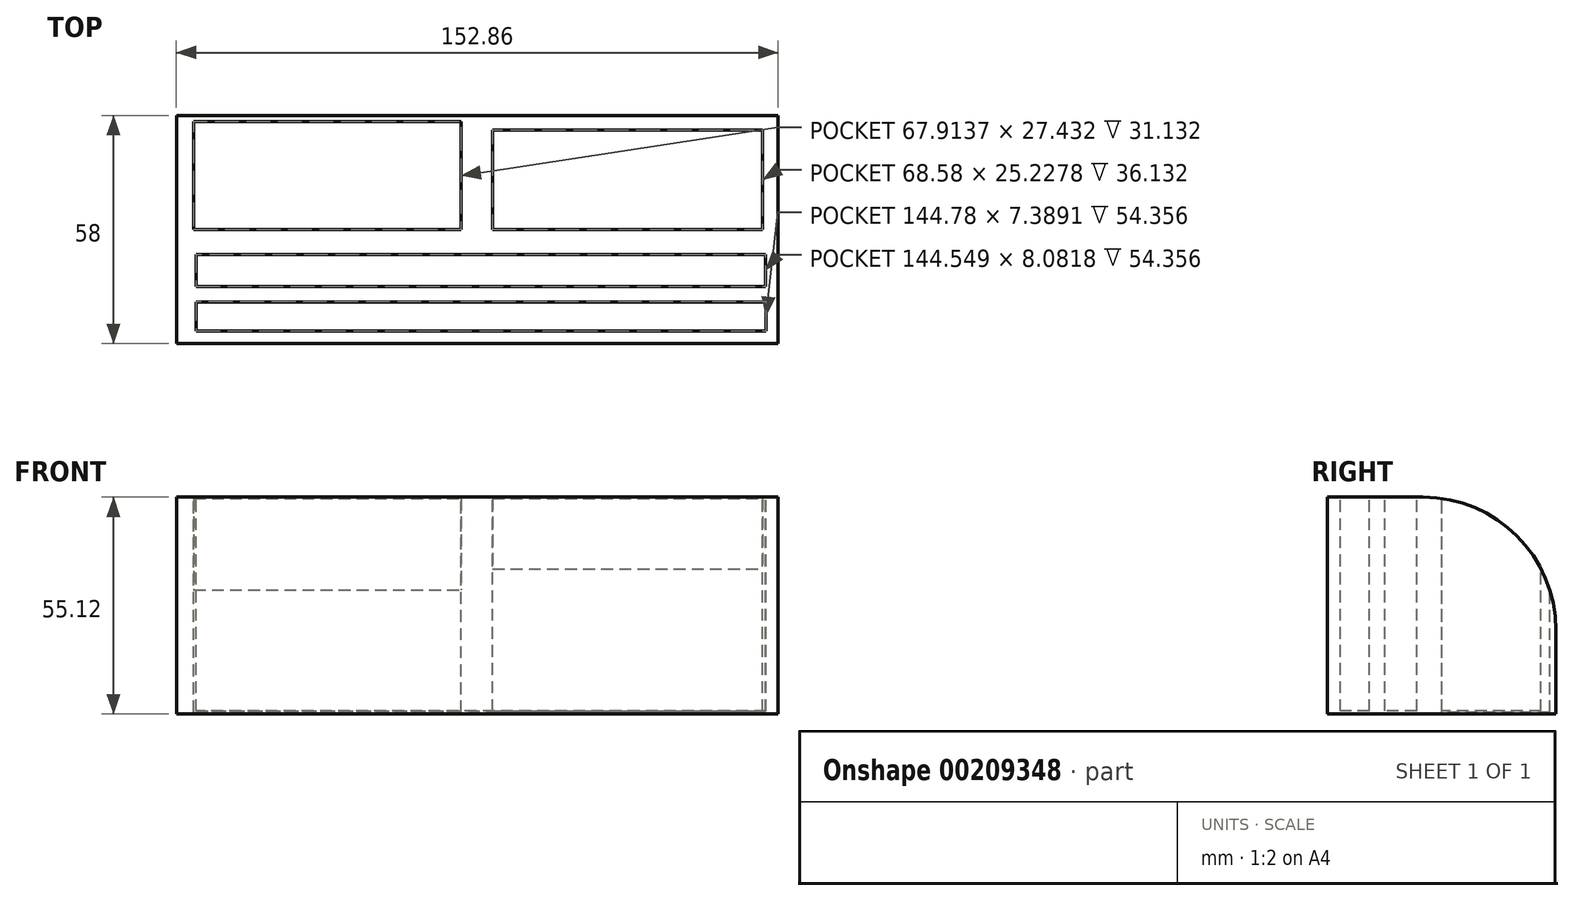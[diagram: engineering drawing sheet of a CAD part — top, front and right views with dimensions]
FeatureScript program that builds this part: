
annotation { "Feature Type Name" : "Feature", "Feature Type Description" : "" }
export const myFeature = defineFeature(function(context is Context, id is Id, definition is map)
    precondition{}
    {
        {
            var Q0;
            Q0=qCreatedBy(makeId("Top.planeOp"),FACE);
            var sketch = newSketch(context, id + "F0", { "sketchPlane" : qUnion([Q0])});
            skLineSegment(sketch, "E0.bottom", {"start": v(-76.43, 29) * mm, "end": v(76.43, 29) * mm});
            skLineSegment(sketch, "E0.top", {"start": v(-76.43, -29) * mm, "end": v(76.43, -29) * mm});
            skLineSegment(sketch, "E0.left", {"start": v(-76.43, 29) * mm, "end": v(-76.43, -29) * mm});
            skLineSegment(sketch, "E0.right", {"start": v(76.43, 29) * mm, "end": v(76.43, -29) * mm});
            skPoint(sketch, "E0.middle", {"position": v(0, 0) * mm});
            skSolve(sketch);
        }
        {
            var Q0;
            Q0=makeQuery(id+"F0.imprint","IMPRINT",FACE,{"disambiguationData":[TD([[makeQuery(id+"F0.imprint","IMPRINT",EDGE,{"derivedFrom":sQuery(id+"F0.wireOp",EDGE,"E0.bottom")}),-1.0]])]});
            extrude(context, id + "F1", {"entities" : qUnion([Q0]), "depth" : 55.12 * mm});
        }
        {
            var Q0;
            Q0=makeQuery(id+"F1.opExtrude","CAP_EDGE",EDGE,{"disambiguationData":[OSD([sQuery(id+"F0.wireOp",EDGE,"E0.bottom")])],"isStart":false});
            fillet(context, id + "F2", {"entities" : qUnion([Q0]), "radius" : 33.73 * mm, "tangentPropagation" : true, "allowEdgeOverflow" : false});
        }
        {
            var Q0;
            Q0=makeQuery(id+"F1.opExtrude","CAP_FACE",FACE,{"disambiguationData":[OSD([sQuery(id+"F0.wireOp",EDGE,"E0.bottom"),sQuery(id+"F0.wireOp",EDGE,"E0.top"),sQuery(id+"F0.wireOp",EDGE,"E0.left"),sQuery(id+"F0.wireOp",EDGE,"E0.right")])],"isStart":false});
            var sketch = newSketch(context, id + "F3", { "sketchPlane" : qUnion([Q0])});
            skLineSegment(sketch, "E1.bottom", {"start": v(-72, 25.23) * mm, "end": v(-4.08, 25.23) * mm});
            skLineSegment(sketch, "E1.top", {"start": v(-72, 0) * mm, "end": v(-4.08, 0) * mm});
            skLineSegment(sketch, "E1.left", {"start": v(-72, 25.23) * mm, "end": v(-72, 0) * mm});
            skLineSegment(sketch, "E1.right", {"start": v(-4.08, 25.23) * mm, "end": v(-4.08, 0) * mm});
            skLineSegment(sketch, "E2.bottom", {"start": v(3.93, 25.23) * mm, "end": v(72.5, 25.23) * mm});
            skLineSegment(sketch, "E2.top", {"start": v(3.93, 0) * mm, "end": v(72.5, 0) * mm});
            skLineSegment(sketch, "E2.left", {"start": v(3.93, 25.23) * mm, "end": v(3.93, 0) * mm});
            skLineSegment(sketch, "E2.right", {"start": v(72.5, 25.23) * mm, "end": v(72.5, 0) * mm});
            skSolve(sketch);
        }
        {
            var Q0;
            Q0=makeQuery(id+"F3.imprint","IMPRINT",FACE,{"disambiguationData":[TD([[makeQuery(id+"F3.imprint","IMPRINT",EDGE,{"derivedFrom":sQuery(id+"F3.wireOp",EDGE,"E1.bottom")}),-1.0]])]});
            extrude(context, id + "F4", {"entities" : qUnion([Q0]), "operationType" : NewBodyOperationType.REMOVE, "oppositeDirection" : true, "depth" : 48.26 * mm});
        }
        {
            var Q0;
            Q0=makeQuery(id+"F4.boolean.opBoolean","COPY",FACE,{"derivedFrom":makeQuery(id+"F4.opExtrude","SWEPT_FACE",FACE,{"disambiguationData":[OSD([sQuery(id+"F3.wireOp",EDGE,"E1.top")])]})});
            extrude(context, id + "F5", {"entities" : qUnion([Q0]), "operationType" : NewBodyOperationType.ADD, "depth" : 27.43 * mm});
        }
        {
            var Q0;
            Q0=makeQuery(id+"F5.opExtrude","SWEPT_FACE",FACE,{"disambiguationData":[OSD([sQuery(id+"F0.wireOp",EDGE,"E0.bottom"),sQuery(id+"F3.wireOp",EDGE,"E1.top")])]});
            var sketch = newSketch(context, id + "F6", { "sketchPlane" : qUnion([Q0])});
            skSolve(sketch);
        }
        {
            var Q0;
            {var subQ0=sQuery(id+"F3.wireOp",EDGE,"E1.top");var subQ1=sQuery(id+"F0.wireOp",EDGE,"E0.bottom");Q0=makeQuery(id+"F6.imprint","IMPRINT",FACE,{"disambiguationData":[TD([[makeQuery(id+"F6.imprint","IMPRINT",EDGE,{"derivedFrom":makeQuery(id+"F5.opExtrude","CAP_EDGE",EDGE,{"disambiguationData":[OSD([subQ1,subQ0])],"isStart":false})}),-1.0]])]});}
            extrude(context, id + "F7", {"entities" : qUnion([Q0]), "operationType" : NewBodyOperationType.REMOVE, "oppositeDirection" : true, "depth" : 54.36 * mm});
        }
        {
            var Q0;
            Q0 = qSketchRegion(id + "F3", true);
            extrude(context, id + "F8", {"entities" : qUnion([Q0]), "operationType" : NewBodyOperationType.REMOVE, "oppositeDirection" : true, "depth" : 54.36 * mm});
        }
        {
            var Q0;
            Q0=makeQuery(id+"F1.opExtrude","CAP_FACE",FACE,{"disambiguationData":[OSD([sQuery(id+"F0.wireOp",EDGE,"E0.bottom"),sQuery(id+"F0.wireOp",EDGE,"E0.top"),sQuery(id+"F0.wireOp",EDGE,"E0.left"),sQuery(id+"F0.wireOp",EDGE,"E0.right")])],"isStart":false});
            var sketch = newSketch(context, id + "F9", { "sketchPlane" : qUnion([Q0])});
            skLineSegment(sketch, "E3.bottom", {"start": v(-71.35, -6.35) * mm, "end": v(73.2, -6.35) * mm});
            skLineSegment(sketch, "E3.top", {"start": v(-71.35, -14.43) * mm, "end": v(73.2, -14.43) * mm});
            skLineSegment(sketch, "E3.left", {"start": v(-71.35, -6.35) * mm, "end": v(-71.35, -14.43) * mm});
            skLineSegment(sketch, "E3.right", {"start": v(73.2, -6.35) * mm, "end": v(73.2, -14.43) * mm});
            skLineSegment(sketch, "E4.bottom", {"start": v(73.43, -18.36) * mm, "end": v(-71.35, -18.36) * mm});
            skLineSegment(sketch, "E4.top", {"start": v(73.43, -25.75) * mm, "end": v(-71.35, -25.75) * mm});
            skLineSegment(sketch, "E4.left", {"start": v(73.43, -18.36) * mm, "end": v(73.43, -25.75) * mm});
            skLineSegment(sketch, "E4.right", {"start": v(-71.35, -18.36) * mm, "end": v(-71.35, -25.75) * mm});
            skSolve(sketch);
        }
        {
            var Q0;
            Q0 = qSketchRegion(id + "F9", true);
            extrude(context, id + "F10", {"entities" : qUnion([Q0]), "operationType" : NewBodyOperationType.REMOVE, "oppositeDirection" : true, "depth" : 54.36 * mm});
        }
    });
